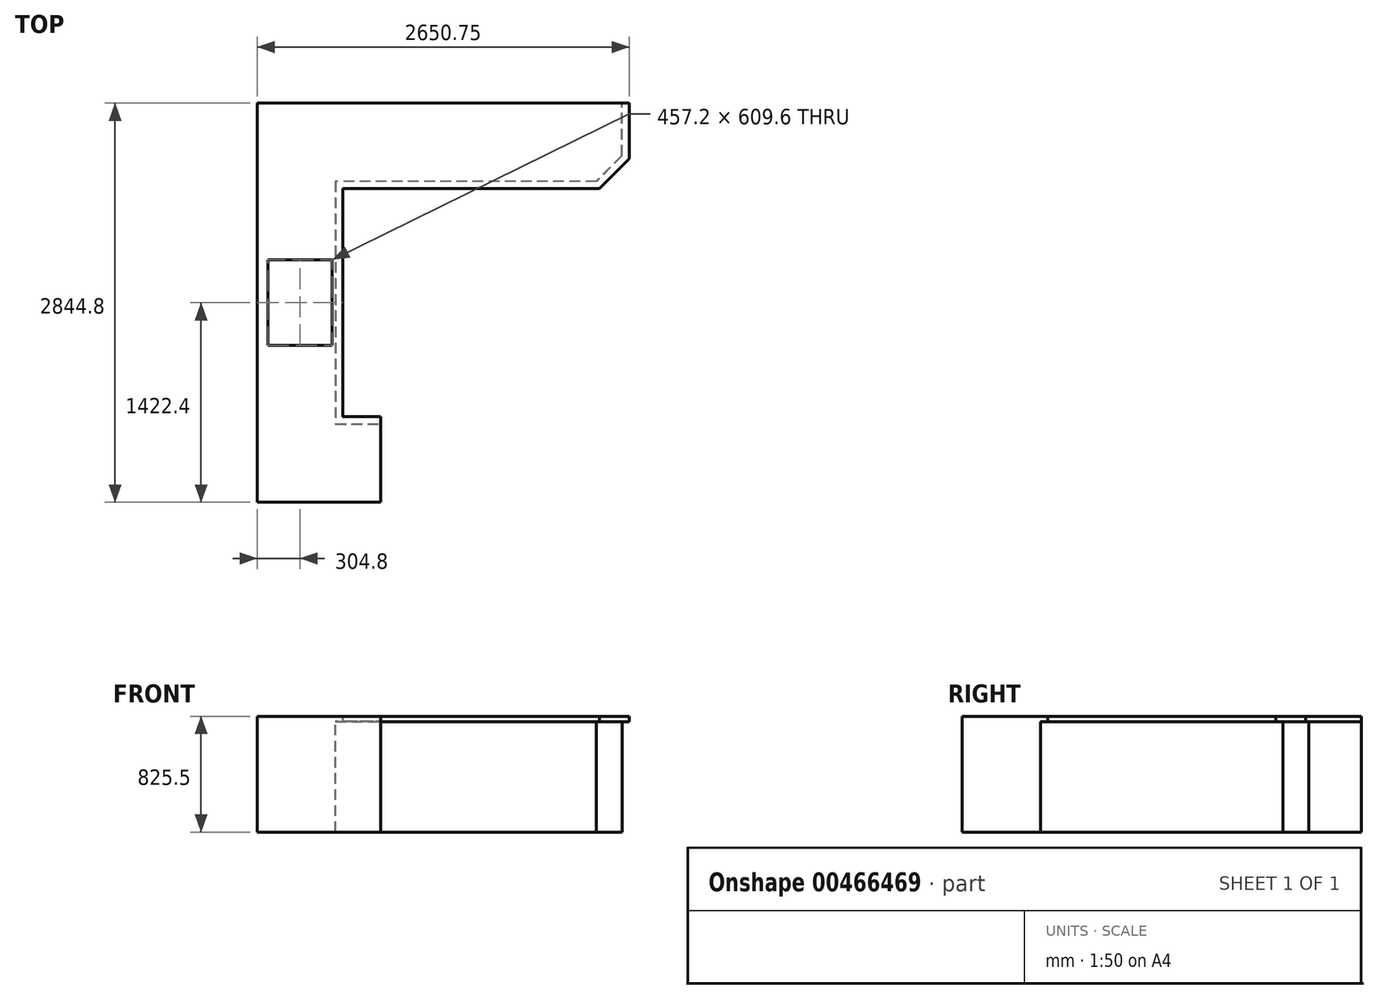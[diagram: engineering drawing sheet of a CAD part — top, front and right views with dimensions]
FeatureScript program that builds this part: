
annotation { "Feature Type Name" : "Feature", "Feature Type Description" : "" }
export const myFeature = defineFeature(function(context is Context, id is Id, definition is map)
    precondition{}
    {
        {
            var Q0;
            Q0=qCreatedBy(makeId("Top.planeOp"),FACE);
            var sketch = newSketch(context, id + "F0", { "sketchPlane" : qUnion([Q0])});
            skLineSegment(sketch, "E0", {"start": v(0, 0) * mm, "end": v(0, 2844.8) * mm});
            skLineSegment(sketch, "E1", {"start": v(0, 2844.8) * mm, "end": v(2650.75, 2844.8) * mm});
            skLineSegment(sketch, "E2", {"start": v(2650.75, 2844.8) * mm, "end": v(2650.75, 2449.14) * mm});
            skLineSegment(sketch, "E3", {"start": v(2436.81, 2235.2) * mm, "end": v(609.6, 2235.2) * mm});
            skLineSegment(sketch, "E4", {"start": v(609.6, 2235.2) * mm, "end": v(609.6, 609.6) * mm});
            skLineSegment(sketch, "E5", {"start": v(609.6, 609.6) * mm, "end": v(877.84, 609.6) * mm});
            skLineSegment(sketch, "E6", {"start": v(877.84, 609.6) * mm, "end": v(877.84, 0) * mm});
            skLineSegment(sketch, "E7", {"start": v(877.84, 0) * mm, "end": v(0, 0) * mm});
            skLineSegment(sketch, "E8", {"start": v(2650.75, 2449.14) * mm, "end": v(2436.81, 2235.2) * mm});
            skSolve(sketch);
        }
        {
            var Q0;
            Q0=makeQuery(id+"F0.imprint","IMPRINT",FACE,{"disambiguationData":[TD([[makeQuery(id+"F0.imprint","IMPRINT",EDGE,{"derivedFrom":sQuery(id+"F0.wireOp",EDGE,"E0")}),-1.0]])]});
            extrude(context, id + "F1", {"entities" : qUnion([Q0]), "depth" : 38.1 * mm});
        }
        {
            var Q0;
            Q0=makeQuery(id+"F1.opExtrude","CAP_FACE",FACE,{"disambiguationData":[OSD([sQuery(id+"F0.wireOp",EDGE,"E0"),sQuery(id+"F0.wireOp",EDGE,"E1"),sQuery(id+"F0.wireOp",EDGE,"E2"),sQuery(id+"F0.wireOp",EDGE,"E3"),sQuery(id+"F0.wireOp",EDGE,"E4"),sQuery(id+"F0.wireOp",EDGE,"E5"),sQuery(id+"F0.wireOp",EDGE,"E6"),sQuery(id+"F0.wireOp",EDGE,"E7"),sQuery(id+"F0.wireOp",EDGE,"E8")])],"isStart":true});
            var sketch = newSketch(context, id + "F2", { "sketchPlane" : qUnion([Q0])});
            skLineSegment(sketch, "E9.0", {"start": v(558.8, -558.8) * mm, "end": v(827.04, -558.8) * mm});
            skLineSegment(sketch, "E9.1", {"start": v(558.8, -2286) * mm, "end": v(558.8, -558.8) * mm});
            skLineSegment(sketch, "E9.2", {"start": v(827.04, -558.8) * mm, "end": v(827.04, 0) * mm});
            skLineSegment(sketch, "E9.3", {"start": v(2415.77, -2286) * mm, "end": v(558.8, -2286) * mm});
            skLineSegment(sketch, "E9.4", {"start": v(2599.95, -2470.18) * mm, "end": v(2415.77, -2286) * mm});
            skLineSegment(sketch, "E10", {"start": v(2599.95, -2470.18) * mm, "end": v(2599.95, -2844.8) * mm});
            skLineSegment(sketch, "E11", {"start": v(827.04, 0) * mm, "end": v(0, 0) * mm});
            skLineSegment(sketch, "E12", {"start": v(0, 0) * mm, "end": v(0, -2844.8) * mm});
            skLineSegment(sketch, "E13", {"start": v(0, -2844.8) * mm, "end": v(2599.95, -2844.8) * mm});
            skSolve(sketch);
        }
        {
            var Q0;
            Q0=makeQuery(id+"F2.imprint","IMPRINT",FACE,{"disambiguationData":[TD([[makeQuery(id+"F2.imprint","IMPRINT",EDGE,{"derivedFrom":sQuery(id+"F2.wireOp",EDGE,"E9.0")}),1.0]])]});
            extrude(context, id + "F3", {"entities" : qUnion([Q0]), "operationType" : NewBodyOperationType.ADD, "depth" : 787.4 * mm});
        }
        {
            var Q0;
            Q0=makeQuery(id+"F3.opExtrude","SWEPT_FACE",FACE,{"disambiguationData":[OSD([sQuery(id+"F2.wireOp",EDGE,"E9.2")])]});
            extrude(context, id + "F4", {"entities" : qUnion([Q0]), "operationType" : NewBodyOperationType.ADD, "depth" : 50.8 * mm});
        }
        {
            var Q0;
            {var subQ0=sQuery(id+"F2.wireOp",EDGE,"E9.2");Q0=makeQuery(id+"F4.boolean.opBoolean","MERGE",FACE,{"derivedFrom":[makeQuery(id+"F3.opExtrude","CAP_FACE",FACE,{"disambiguationData":[OSD([sQuery(id+"F2.wireOp",EDGE,"E9.0"),sQuery(id+"F2.wireOp",EDGE,"E9.1"),subQ0,sQuery(id+"F2.wireOp",EDGE,"E9.3"),sQuery(id+"F2.wireOp",EDGE,"E9.4"),sQuery(id+"F2.wireOp",EDGE,"E10"),sQuery(id+"F2.wireOp",EDGE,"E11"),sQuery(id+"F2.wireOp",EDGE,"E12"),sQuery(id+"F2.wireOp",EDGE,"E13")])],"isStart":false}),makeQuery(id+"F4.opExtrude","SWEPT_FACE",FACE,{"disambiguationData":[OSD([subQ0]),TDD([makeQuery(id+"F3.opExtrude","CAP_EDGE",EDGE,{"disambiguationData":[OSD([subQ0])],"isStart":false})])]})]});}
            shell(context, id + "F5", {"entities" : qUnion([Q0]), "thickness" : 2.54 * mm});
        }
        {
            var Q0;
            Q0=makeQuery(id+"F1.opExtrude","CAP_FACE",FACE,{"disambiguationData":[OSD([sQuery(id+"F0.wireOp",EDGE,"E0"),sQuery(id+"F0.wireOp",EDGE,"E1"),sQuery(id+"F0.wireOp",EDGE,"E2"),sQuery(id+"F0.wireOp",EDGE,"E3"),sQuery(id+"F0.wireOp",EDGE,"E4"),sQuery(id+"F0.wireOp",EDGE,"E5"),sQuery(id+"F0.wireOp",EDGE,"E6"),sQuery(id+"F0.wireOp",EDGE,"E7"),sQuery(id+"F0.wireOp",EDGE,"E8")])],"isStart":false});
            var sketch = newSketch(context, id + "F6", { "sketchPlane" : qUnion([Q0])});
            skLineSegment(sketch, "E14", {"start": v(609.6, 1422.4) * mm, "end": v(0, 1422.4) * mm, "construction": true});
            skLineSegment(sketch, "E15.bottom", {"start": v(76.2, 1117.6) * mm, "end": v(533.4, 1117.6) * mm});
            skLineSegment(sketch, "E15.top", {"start": v(76.2, 1727.2) * mm, "end": v(533.4, 1727.2) * mm});
            skLineSegment(sketch, "E15.left", {"start": v(76.2, 1117.6) * mm, "end": v(76.2, 1727.2) * mm});
            skLineSegment(sketch, "E15.right", {"start": v(533.4, 1117.6) * mm, "end": v(533.4, 1727.2) * mm});
            skSolve(sketch);
        }
        {
            var Q0;
            Q0=makeQuery(id+"F6.imprint","IMPRINT",FACE,{"disambiguationData":[TD([[makeQuery(id+"F6.imprint","IMPRINT",EDGE,{"derivedFrom":sQuery(id+"F6.wireOp",EDGE,"E15.bottom")}),1.0]])]});
            extrude(context, id + "F7", {"entities" : qUnion([Q0]), "operationType" : NewBodyOperationType.REMOVE, "oppositeDirection" : true, "depth" : 304.8 * mm});
        }
    });
